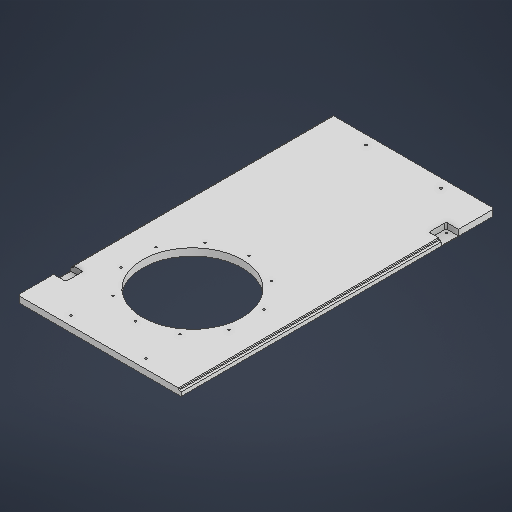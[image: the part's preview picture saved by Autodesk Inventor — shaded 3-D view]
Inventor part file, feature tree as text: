
AUTODESK INVENTOR PART (.ipt)
format: ipt  version: 2025 (Build 290162000, 162)  size: 343,040 bytes
history: native  units: in
note: dims shown in document units (in); Inventor stores cm internally (conversion verified against a paired STEP export)
features: sketch x9, chamfer x5, extrude x4, hole x3, plane x2, fillet x1
ambient origin geometry x8: Origin, YZ Plane, XZ Plane, XY Plane, X Axis, Y Axis, Z Axis, Center Point
bodies: Solid1 (feature_tree)
feature tree (24):
  extrude  "Extrusion1"  Depth=27.1654in
  sketch  "Sketch2"  dims[d2=0.625in d3=0.0in d4=8.0709in]
  extrude  "Extrusion2"  Depth=0.625in
  plane  "Work Plane1"
  hole  "Hole3"  [1 undecoded]
  sketch  "Sketch7"  dims[d56=25.5906in]
  plane  "Work Plane2"
  hole  "Hole4"  [1 undecoded]
  sketch  "Sketch9"  dims[d64=10.3543in]
  fillet  "Fillet2"  Radius=6.5in
  chamfer  "Chamfer1"  Distance=1.063in
  chamfer  "Chamfer2"  Distance=1.063in
  extrude  "Extrusion7"  Depth=1.4961in
  extrude  "Extrusion8"  Depth=1.4961in
  chamfer  "Chamfer3"  Distance=3.1102in
  chamfer  "Chamfer4"  Distance=3.1102in
  hole  "Hole5"  [1 undecoded]
  chamfer  "Chamfer5"  Distance=0.0984in Angle=45.0deg
  sketch  "Sketch1"  dims[d0=14.1732in d1=27.1654in]
  sketch  "Sketch6"  dims[d8=10.6299in d50=5.9055in d55=6.5in]
  sketch  "Sketch8"  dims[d57=0.1936in d58=0.1969in d59=0.1575in d60=0.0787in d61=90.0deg d62=0.1969in d63=0.8108in]
  sketch  "Sketch10"  dims[d65=10.6299in]
  sketch  "Sketch11"  dims[d68=9.8425in d74=0.1628in d75=0.3937in d76=0.1575in d77=0.0787in d78=90.0deg d79=0.3937in d80=0.8108in d82=1.063in d83=1.063in d84=1.4961in d85=1.4961in d86=3.1102in d87=3.1102in d88=0.1969in d89=0.0984in d90=0.0787in d91=45.0deg d92=0.0984in d93=0.0787in d94=45.0deg d95=0.1181in d96=0.1181in d97=0.4951in d98=0.0in d99=0.2362in d100=0.2362in d101=0.122in d102=0.0in d103=0.0787in d104=0.1378in d105=45.0deg d106=0.1378in d107=0.0787in d108=45.0deg d109=0.748in d110=0.315in d111=0.8661in d112=0.748in d113=0.1299in d114=0.1299in d115=0.1299in d116=0.1299in d118=0.315in d119=0.8661in d120=0.748in d121=0.748in d122=0.1276in d123=0.315in d124=0.1575in d125=0.0787in d126=90.0deg d127=0.315in d128=0.8108in d129=0.0138in d130=0.0787in d131=45.0deg d146=0.1969in d147=3.937in d149=360.0deg d26=0.0394in d27=0.0394in d28=0.0394in d29=0.0059in d30=0.0098in d31=0.0148in d32=0.5635in d33=0.0295in d34=0.8108in d35=0.0025in d36=0.0295in d37=0.0148in d66=0.0197in d67=0.0344in]
  sketch  "Sketch Circular Pattern5"  dims[d5=8.6614in d6=0.0in d7=0.0in]
note: 3 required parameter values undecoded (feature->parameter linkage not recoverable at this tier; creation-order binding heuristic only, values carry confidence <= 0.55)
